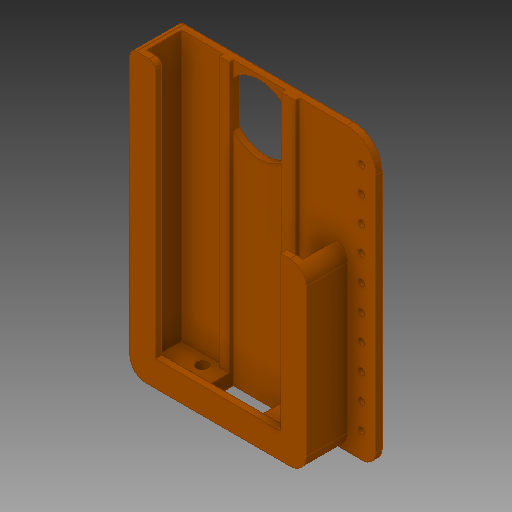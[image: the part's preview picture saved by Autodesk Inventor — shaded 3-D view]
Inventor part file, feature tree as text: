
AUTODESK INVENTOR PART (.ipt)
format: ipt  version: 2019 (Build 230136000, 136)  size: 351,232 bytes
history: native  units: in
note: dims shown in document units (in); Inventor stores cm internally (conversion verified against a paired STEP export)
features: sketch x17, extrude x15, fillet x8, projected_geometry x5, hole x1, pattern_linear x1
ambient origin geometry x8: Origin, YZ Plane, XZ Plane, XY Plane, X Axis, Y Axis, Z Axis, Center Point
bodies: Solid1 (feature_tree), body (feature_tree)
feature tree (47):
  extrude  "Extrusion2"  Depth=5.5in
  extrude  "Extrusion3"  Depth=0.5in
  extrude  "Extrusion4"  Depth=0.5in
  extrude  "Extrusion5"  Depth=0.2in
  extrude  "Extrusion6"  Depth=0.125in
  extrude  "Extrusion7"  Depth=3.0375in
  fillet  "Fillet1"  Radius=0.125in
  fillet  "Fillet2"  Radius=2.0in
  fillet  "Fillet3"  Radius=0.65in
  hole  "Hole1"  [1 undecoded]
  pattern_linear  "Rectangular Pattern1"  Count1=10 Spacing1=0.5in
  extrude  "Extrusion8"  Depth=0.25in
  sketch  "Sketch14"  dims[d27=3.5in d28=0.0in]
  fillet  "Fillet4"  Radius=4.0in
  fillet  "Fillet5"  Radius=0.25in
  fillet  "Fillet6"  Radius=0.5in
  extrude  "Extrusion13"  Depth=0.125in
  extrude  "Extrusion14"  Depth=1.6171in
  extrude  "Extrusion15"  Depth=1.615in
  extrude  "Extrusion17"  Depth=0.805in
  extrude  "Extrusion18"  Depth=0.805in
  extrude  "Extrusion19"  Depth=1.0in TaperAngle=0.0deg
  extrude  "Extrusion20"  Depth=1.0in TaperAngle=0.0deg
  extrude  "Extrusion21"  Depth=0.5065in
  fillet  "Fillet7"  Radius=1.0in
  fillet  "Fillet8"  Radius=1.35in
  sketch  "Sketch1"  dims[d0=3.4375in d1=5.5in]
  sketch  "Sketch2"  dims[d2=0.93in d3=0.0in d4=0.5in]
  sketch  "Sketch4"  dims[d5=0.5in d6=0.5in]
  sketch  "Sketch6"  dims[d7=0.65in d8=0.0in d9=0.2in]
  projected_geometry  "Projected Loop2"
  sketch  "Sketch7"  dims[d10=0.2in d12=0.125in]
  projected_geometry  "Projected Loop3"
  sketch  "Sketch8"  dims[d13=5.25in d14=0.0in d15=3.0375in d17=0.125in d18=2.0in d19=0.65in d20=0.0in]
  sketch  "Sketch9"  dims[d21=0.55in d22=0.0in d23=0.8in]
  sketch  "Sketch13"  dims[d24=5.5in d25=0.0in]
  sketch  "Sketch18"  dims[d29=0.5625in]
  sketch  "Sketch19"  dims[d30=0.3125in]
  projected_geometry  "Projected Loop5"
  sketch  "Sketch20"  dims[d31=0.3125in]
  sketch  "Sketch21"  dims[d32=0.275in d33=1.0in]
  projected_geometry  "Projected Loop6"
  projected_geometry  "Projected Loop7"
  sketch  "Sketch22"  dims[d34=0.13in d35=0.75in d36=0.375in d37=0.25in d38=0.5635in d39=1.0in d40=0.8108in d41=3.937in d43=0.5in]
  sketch  "Sketch24"  dims[d44=0.9in d45=0.9in d46=4.0in d47=0.0in d56=0.25in d57=0.5in]
  sketch  "Sketch26"  dims[d58=0.125in d59=0.125in]
  sketch  "Sketch28"  dims[d60=0.08in d61=0.0in d63=1.6171in d64=1.615in d65=0.805in d66=0.805in d67=1.0in d68=0.0in d69=1.0in d70=0.0in d73=0.5065in d74=1.0in d75=0.0in d76=1.35in d77=0.5065in d78=1.0in d79=0.0in d80=1.0in d81=0.0in d82=1.0in d83=0.0in d84=0.75in d85=1.0in d86=0.0in d87=0.125in d88=0.3125in]
note: 1 required parameter value undecoded (feature->parameter linkage not recoverable at this tier; creation-order binding heuristic only, values carry confidence <= 0.55)
